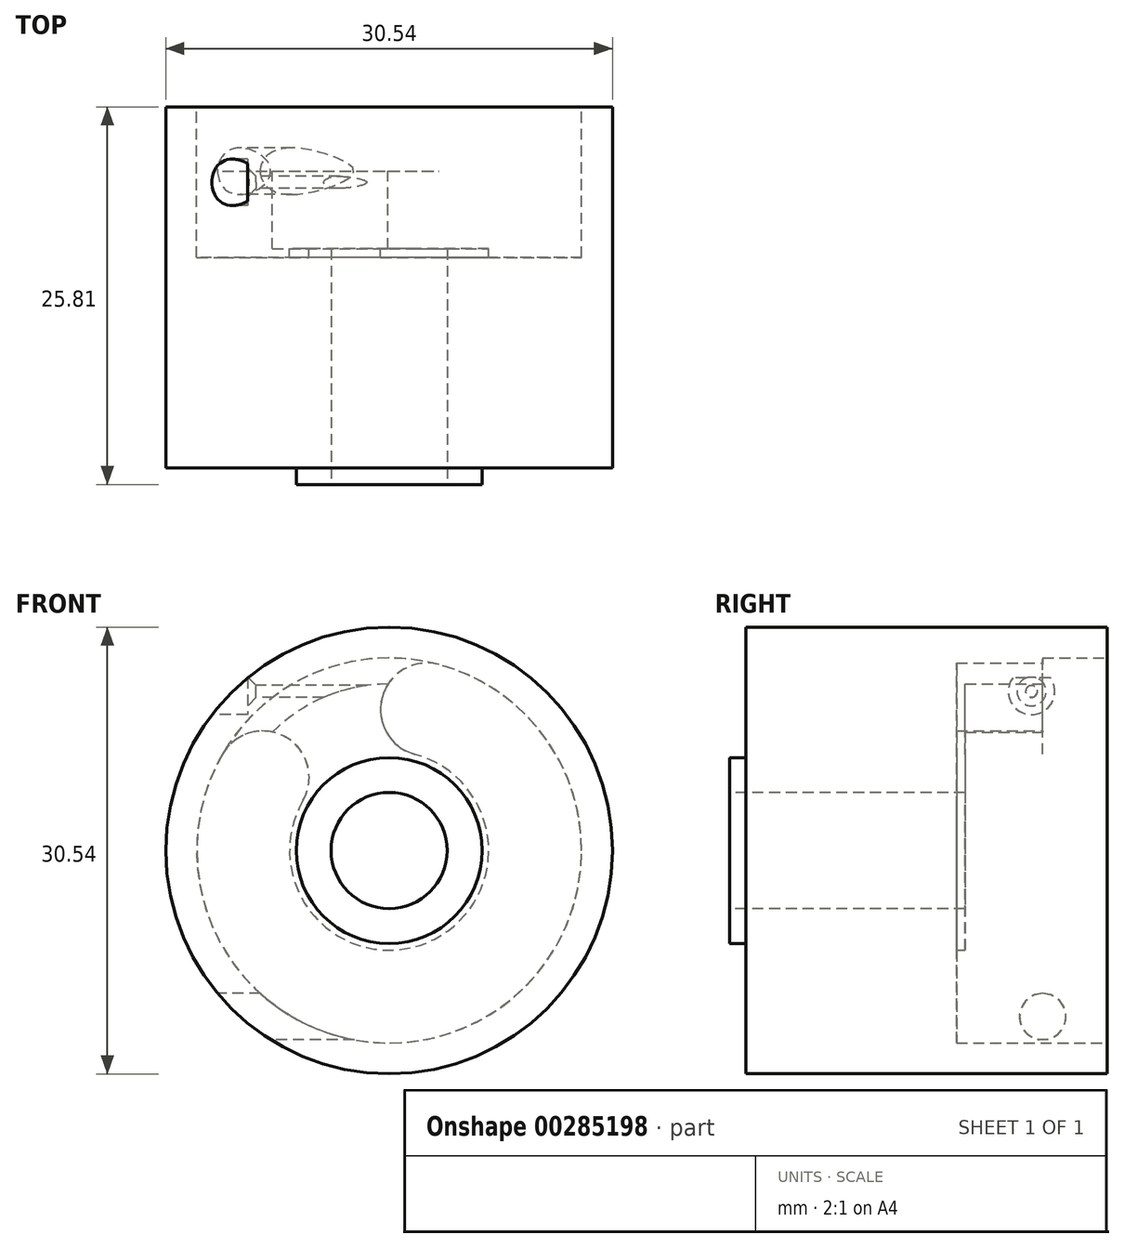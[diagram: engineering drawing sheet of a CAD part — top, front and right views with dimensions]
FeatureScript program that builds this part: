
annotation { "Feature Type Name" : "Feature", "Feature Type Description" : "" }
export const myFeature = defineFeature(function(context is Context, id is Id, definition is map)
    precondition{}
    {
        {
            var Q0;
            Q0=qCreatedBy(makeId("Front.planeOp"),FACE);
            var sketch = newSketch(context, id + "F0", { "sketchPlane" : qUnion([Q0])});
            skCircle(sketch, "E0", {"center": v(0, 0) * mm, "radius": 3.97 * mm});
            skCircle(sketch, "E1", {"center": v(0, 0) * mm, "radius": 15.27 * mm});
            skSolve(sketch);
        }
        {
            var Q0;
            Q0 = qSketchRegion(id + "F0", true);
            extrude(context, id + "F1", {"entities" : qUnion([Q0]), "oppositeDirection" : true, "depth" : 24.7 * mm});
        }
        {
            var Q0;
            Q0=qCreatedBy(makeId("Front.planeOp"),FACE);
            var sketch = newSketch(context, id + "F2", { "sketchPlane" : qUnion([Q0])});
            skCircle(sketch, "E2", {"center": v(0, 0) * mm, "radius": 3.97 * mm});
            skCircle(sketch, "E3", {"center": v(0, 0) * mm, "radius": 6.35 * mm});
            skSolve(sketch);
        }
        {
            var Q0;
            Q0 = qSketchRegion(id + "F2", true);
            extrude(context, id + "F3", {"entities" : qUnion([Q0]), "operationType" : NewBodyOperationType.ADD, "depth" : 1.12 * mm});
        }
        {
            var Q0;
            Q0=makeQuery(id+"F1.opExtrude","CAP_FACE",FACE,{"disambiguationData":[OSD([sQuery(id+"F0.wireOp",EDGE,"E0"),sQuery(id+"F0.wireOp",EDGE,"E1")])],"isStart":false});
            var sketch = newSketch(context, id + "F4", { "sketchPlane" : qUnion([Q0])});
            skCircle(sketch, "E4", {"center": v(0, 0) * mm, "radius": 13.16 * mm});
            skSolve(sketch);
        }
        {
            var Q0;
            Q0 = qSketchRegion(id + "F4", true);
            extrude(context, id + "F5", {"entities" : qUnion([Q0]), "operationType" : NewBodyOperationType.REMOVE, "oppositeDirection" : true, "depth" : 4.4 * mm});
        }
        {
            var Q0;
            Q0=makeQuery(id+"F5.boolean.opBoolean","COPY",FACE,{"derivedFrom":makeQuery(id+"F5.opExtrude","CAP_FACE",FACE,{"disambiguationData":[OSD([sQuery(id+"F4.wireOp",EDGE,"E4")])],"isStart":false})});
            var sketch = newSketch(context, id + "F6", { "sketchPlane" : qUnion([Q0])});
            skCircle(sketch, "E5", {"center": v(0, 0) * mm, "radius": 9.98 * mm, "construction": true});
            skCircle(sketch, "E6", {"center": v(-2.58, 9.64) * mm, "radius": 3.18 * mm});
            skCircle(sketch, "E7", {"center": v(8.64, 5) * mm, "radius": 3.18 * mm});
            skArc(sketch, "E8", {"start": v(-3.4, 12.7) * mm, "mid": v(-5.04, -12.16) * mm, "end": v(11.4, 6.58) * mm});
            skArc(sketch, "E9", {"start": v(-1.76, 6.58) * mm, "mid": v(-2.6, -6.29) * mm, "end": v(5.9, 3.4) * mm});
            skLineSegment(sketch, "E10", {"start": v(0, 0) * mm, "end": v(0, 22.93) * mm, "construction": true});
            skLineSegment(sketch, "E11", {"start": v(0, 0) * mm, "end": v(-2.58, 9.64) * mm, "construction": true});
            skLineSegment(sketch, "E12", {"start": v(0, 0) * mm, "end": v(8.64, 5) * mm, "construction": true});
            skSolve(sketch);
        }
        {
            var Q0;
            Q0 = qSketchRegion(id + "F6", true);
            extrude(context, id + "F7", {"entities" : qUnion([Q0]), "operationType" : NewBodyOperationType.REMOVE, "oppositeDirection" : true, "depth" : 5.9 * mm});
        }
        {
            var Q0;
            Q0=makeQuery(id+"F5.boolean.opBoolean","COPY",FACE,{"derivedFrom":makeQuery(id+"F5.opExtrude","CAP_FACE",FACE,{"disambiguationData":[OSD([sQuery(id+"F4.wireOp",EDGE,"E4")])],"isStart":false})});
            var sketch = newSketch(context, id + "F8", { "sketchPlane" : qUnion([Q0])});
            skCircle(sketch, "E13", {"center": v(0, 0) * mm, "radius": 11.38 * mm});
            skSolve(sketch);
        }
        {
            var Q0;
            Q0 = qSketchRegion(id + "F8", true);
            extrude(context, id + "F9", {"entities" : qUnion([Q0]), "operationType" : NewBodyOperationType.REMOVE, "oppositeDirection" : true, "depth" : 5.3 * mm});
        }
        {
            var Q0;
            Q0=qCreatedBy(makeId("Right.planeOp"),FACE);
            cPlane(context, id + "F10", {"entities" : qUnion([Q0]), "cplaneType" : CPlaneType.OFFSET, "offset" : 15.27 * mm, "oppositeDirection" : true, "width" : 152.4 * mm, "height" : 152.4 * mm});
        }
        {
            var Q0;
            Q0=qCreatedBy(id+"F10.planeOp",FACE);
            var sketch = newSketch(context, id + "F11", { "sketchPlane" : qUnion([Q0]), "disableImprinting" : false});
            skCircle(sketch, "E14", {"center": v(19.53, 10.87) * mm, "radius": 0.4 * mm});
            skCircle(sketch, "E15", {"center": v(20.3, -11.35) * mm, "radius": 1.59 * mm});
            skSolve(sketch);
        }
        {
            var Q0;
            Q0 = qSketchRegion(id + "F11", true);
            extrude(context, id + "F12", {"entities" : qUnion([Q0]), "operationType" : NewBodyOperationType.REMOVE, "depth" : 15.27 * mm, "offsetDistance" : 25.4 * mm});
        }
        {
            var Q0;
            Q0=qCreatedBy(id+"F10.planeOp",FACE);
            var sketch = newSketch(context, id + "F13", { "sketchPlane" : qUnion([Q0])});
            skCircle(sketch, "E16", {"center": v(19.53, 10.87) * mm, "radius": 1.59 * mm});
            skSolve(sketch);
        }
        {
            var Q0;
            Q0 = qSketchRegion(id + "F13", true);
            extrude(context, id + "F14", {"entities" : qUnion([Q0]), "operationType" : NewBodyOperationType.REMOVE, "depth" : 5.6 * mm, "offsetDistance" : 25.4 * mm});
        }
        {
            var Q0;
            Q0=makeQuery(id+"F14.boolean.opBoolean","INTERSECT",EDGE,{"derivedFrom":[makeQuery(id+"F12.boolean.opBoolean","COPY",FACE,{"derivedFrom":makeQuery(id+"F12.opExtrude","SWEPT_FACE",FACE,{"disambiguationData":[OSD([sQuery(id+"F11.wireOp",EDGE,"E14")])]})}),makeQuery(id+"F14.opExtrude","CAP_FACE",FACE,{"disambiguationData":[OSD([sQuery(id+"F13.wireOp",EDGE,"E16")])],"isStart":false})]});
            chamfer(context, id + "F15", {"entities" : qUnion([Q0]), "width" : 0.58 * mm, "tangentPropagation" : true});
        }
    });
